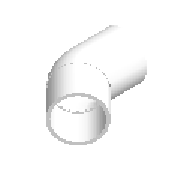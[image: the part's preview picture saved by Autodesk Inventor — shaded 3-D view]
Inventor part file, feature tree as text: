
AUTODESK INVENTOR PART (.ipt)
format: ipt  version: 2023 (Build 270158000, 158)  size: 258,048 bytes
history: native  units: mm (DEFAULTED — no unit token found)
features: revolve x6, other x6, sketch x3
ambient origin geometry x8: Origin, YZ Plane, XZ Plane, XY Plane, X Axis, Y Axis, Z Axis, Center Point
bodies: Solid1 (feature_tree)
feature tree (15):
  sketch  "Sketch1"  dims[d0=61.0mm d1=23.5mm]
  revolve  "Revolution1"  [1 undecoded]
  revolve  "Revolution2"  [1 undecoded]
  revolve  "Revolution3"  [1 undecoded]
  revolve  "Revolution4"  Angle=135.0deg
  sketch  "Sketch2"  dims[d2=110.0mm d3=8.2mm]
  revolve  "Revolution5"  Angle=90.0deg
  revolve  "Revolution6"  Angle=90.0deg
  other  "Work Point1"
  other  "Work Point2"
  other  "Work Axis1"
  other  "Work Point3"
  other  "Work Axis2"
  other  "Work Point4"
  sketch  "Sketch3"  dims[d4=8.2mm d5=110.0mm d6=135.0deg d139=90.0deg d140=90.0deg d7=61.0mm d8=23.5mm d9=3.995mm d10=3.995mm d11=104.5mm d203=7.845255mm d12=104.5mm d205=7.845255mm d13=104.5mm d14=126.4mm d15=0.01mm d16=45.0deg d17=6.0mm d18=220.0mm d19=45.0deg]
note: 3 required parameter values undecoded (feature->parameter linkage not recoverable at this tier; creation-order binding heuristic only, values carry confidence <= 0.55)
